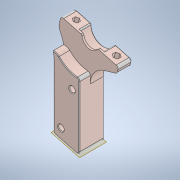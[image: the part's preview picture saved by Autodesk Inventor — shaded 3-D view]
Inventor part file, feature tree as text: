
AUTODESK INVENTOR PART (.ipt)
format: ipt  version: 2021.2 (Build 252289000, 289)  size: 397,312 bytes
history: native  units: mm
features: other x6, chamfer x2, fillet x1
ambient origin geometry x8: Origin, YZ Plane, XZ Plane, XY Plane, X Axis, Y Axis, Z Axis, Center Point
bodies: Body1 (feature_tree)
feature tree (9):
  other  "Твёрдое тело.ipt"
  other  "РабПлоскость1"
  other  "Разделение1"
  fillet  "Сопряжение1"  Radius=10.0mm
  chamfer  "Фаска1"  Distance=2.0mm
  chamfer  "Фаска2"  Distance=2.0mm
  other  "Ножка 2::Твёрдое тело.ipt"
  other  "Элемент создания тегов1"
  other  "Твердое тело1"
